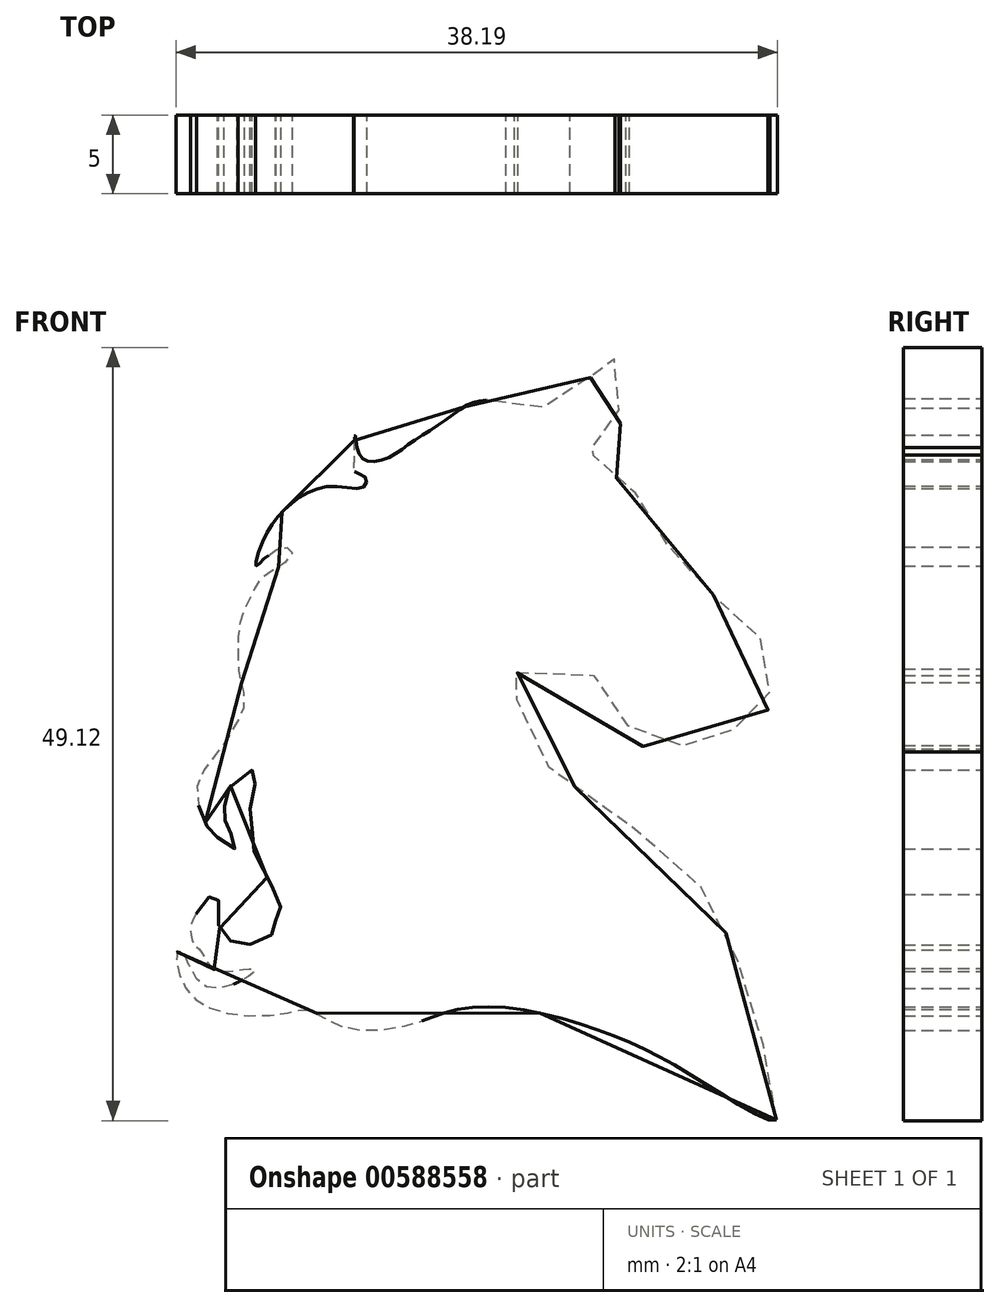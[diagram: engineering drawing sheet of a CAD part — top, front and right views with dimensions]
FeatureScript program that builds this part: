
annotation { "Feature Type Name" : "Feature", "Feature Type Description" : "" }
export const myFeature = defineFeature(function(context is Context, id is Id, definition is map)
    precondition{}
    {
        {
            var Q0;
            Q0=qCreatedBy(makeId("Front.planeOp"),FACE);
            var sketch = newSketch(context, id + "F0", { "sketchPlane" : qUnion([Q0])});
            skFitSpline(sketch, "E0", {"points": [v(-11.4, 5.98) * mm, v(-11.8, 7.87) * mm, v(-12.13, 10.26) * mm, v(-12.8, 12.73) * mm, v(-13.67, 15.6) * mm, v(-14.88, 18.46) * mm, v(-15.98, 20.52) * mm, v(-17.53, 22.06) * mm, v(-20.03, 24.17) * mm, v(-23.62, 26.76) * mm, v(-26.6, 29.06) * mm, v(-28.01, 31.32) * mm, v(-27.84, 32.88) * mm, v(-28.01, 33.9) * mm, v(-28.52, 34.23) * mm, v(-28.52, 34.6) * mm, v(-27.13, 34.02) * mm, v(-24.3, 33.9) * mm, v(-22.66, 34.19) * mm, v(-20.77, 32.8) * mm, v(-20.94, 31.5) * mm, v(-19.97, 29.77) * mm, v(-18.75, 29.6) * mm, v(-17.1, 29.72) * mm, v(-15.76, 29.35) * mm, v(-14.7, 30.23) * mm, v(-13.65, 31.11) * mm, v(-12.3, 31.87) * mm, v(-11.88, 32.08) * mm, v(-11.88, 33.8) * mm, v(-11.92, 35.45) * mm, v(-12.02, 36.15) * mm, v(-12.55, 36.68) * mm, v(-13.7, 37.46) * mm, v(-15, 38.89) * mm, v(-15.61, 39.51) * mm, v(-17.7, 41.69) * mm, v(-18.26, 42.32) * mm, v(-18.46, 43.7) * mm, v(-19.23, 44.93) * mm, v(-20.57, 45.93) * mm, v(-21.67, 46.94) * mm, v(-22.24, 48.1) * mm, v(-23.58, 48.04) * mm, v(-24.45, 48) * mm, v(-24.38, 48.57) * mm, v(-22.98, 48.7) * mm, v(-21.74, 49.28) * mm, v(-21.3, 50.08) * mm, v(-21.39, 50.85) * mm, v(-21.45, 52.42) * mm, v(-21.67, 53.21) * mm, v(-21.64, 53.64) * mm, v(-21.8, 54.67) * mm, v(-22.2, 55.05) * mm, v(-22.64, 54.63) * mm, v(-22.92, 53.55) * mm, v(-23.6, 52.8) * mm, v(-24.6, 52.02) * mm, v(-25.97, 51.3) * mm, v(-27.2, 51.3) * mm, v(-27.93, 51.7) * mm, v(-29.66, 51.72) * mm, v(-30.92, 51.45) * mm, v(-32.65, 50.27) * mm, v(-34.6, 48.98) * mm, v(-36.06, 48.04) * mm, v(-37.49, 47.87) * mm, v(-38.02, 48.65) * mm, v(-38.14, 49.47) * mm, v(-38.23, 49.1) * mm, v(-38.23, 47.8) * mm, v(-38.16, 47.15) * mm, v(-37.47, 46.77) * mm, v(-37.64, 46.18) * mm, v(-39.38, 46.22) * mm, v(-41.45, 45.66) * mm, v(-43.03, 44.33) * mm, v(-44.12, 42.5) * mm, v(-44.44, 41.17) * mm, v(-43.95, 41.6) * mm, v(-43.45, 41.97) * mm, v(-42.86, 42.33) * mm, v(-42.16, 42.2) * mm, v(-42.27, 41.7) * mm, v(-43.55, 40.77) * mm, v(-44.33, 40.14) * mm, v(-44.69, 39.36) * mm, v(-45.15, 38.5) * mm, v(-45.5, 37.4) * mm, v(-45.6, 35.75) * mm, v(-45.5, 34.14) * mm, v(-45.33, 33.64) * mm, v(-45.21, 32.16) * mm, v(-45.63, 31.32) * mm, v(-46.22, 30.26) * mm, v(-47.33, 28.77) * mm, v(-48.2, 26.94) * mm, v(-47.68, 24.85) * mm, v(-47.42, 24.45) * mm, v(-46.9, 23.92) * mm, v(-45.85, 23.2) * mm, v(-45.66, 23.47) * mm, v(-46.27, 24.47) * mm, v(-46.4, 24.9) * mm, v(-46.44, 25.46) * mm, v(-46.46, 25.96) * mm, v(-46.2, 27.02) * mm, v(-44.55, 28.22) * mm, v(-44.44, 27.66) * mm, v(-44.81, 25.83) * mm, v(-44.7, 24.82) * mm, v(-44.64, 23.36) * mm, v(-44.12, 22.15) * mm, v(-43.7, 21.3) * mm, v(-43.15, 20.22) * mm, v(-42.88, 19.07) * mm, v(-43.2, 18.63) * mm, v(-43.2, 18.1) * mm, v(-44.17, 17.33) * mm, v(-45.46, 17.12) * mm, v(-46.44, 17.65) * mm, v(-46.9, 18.77) * mm, v(-46.87, 20.22) * mm, v(-47.25, 20.25) * mm, v(-48.02, 19.43) * mm, v(-48.58, 18.3) * mm, v(-48.4, 17.14) * mm, v(-47.98, 16.75) * mm, v(-47.18, 15.58) * mm, v(-45.32, 15.52) * mm, v(-44.52, 15.52) * mm, v(-45.48, 14.78) * mm, v(-47.28, 14.36) * mm, v(-48.4, 15.2) * mm, v(-49.2, 16.74) * mm, v(-49.46, 16.64) * mm, v(-49.35, 15.36) * mm, v(-48.4, 13.72) * mm, v(-45.74, 12.66) * mm, v(-42.24, 12.82) * mm, v(-41.07, 12.98) * mm, v(-39, 11.92) * mm, v(-34.87, 11.97) * mm, v(-32.53, 12.76) * mm, v(-28.92, 13.14) * mm, v(-23.35, 11.92) * mm, v(-19.06, 10.11) * mm, v(-14.7, 7.51) * mm, v(-11.4, 5.98) * mm]});
            skSolve(sketch);
        }
        {
            var Q0;
            Q0=makeQuery(id+"F0.imprint","IMPRINT",FACE,{"disambiguationData":[TD([[makeQuery(id+"F0.imprint","IMPRINT",EDGE,{"derivedFrom":sQuery(id+"F0.wireOp",EDGE,"E0")}),1.0]])]});
            extrude(context, id + "F1", {"entities" : qUnion([Q0]), "depth" : 5 * mm, "offsetDistance" : 25 * mm});
        }
    });
